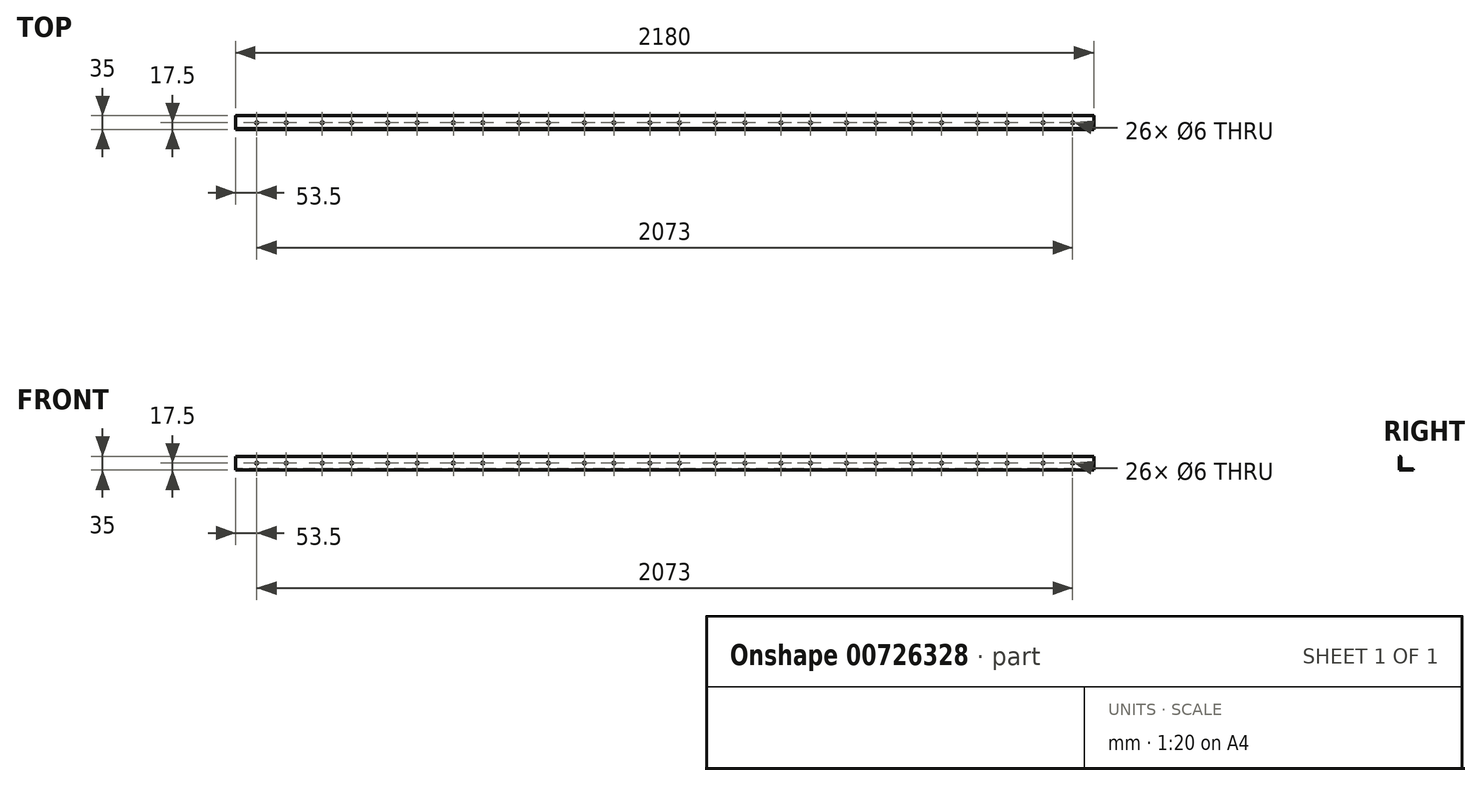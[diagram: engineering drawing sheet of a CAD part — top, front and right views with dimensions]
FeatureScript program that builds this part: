
annotation { "Feature Type Name" : "Feature", "Feature Type Description" : "" }
export const myFeature = defineFeature(function(context is Context, id is Id, definition is map)
    precondition{}
    {
        {
            var Q0;
            Q0=qCreatedBy(makeId("Right.planeOp"),FACE);
            var sketch = newSketch(context, id + "F0", { "sketchPlane" : qUnion([Q0])});
            skLineSegment(sketch, "E0", {"start": v(0, 0) * mm, "end": v(35, 0) * mm});
            skLineSegment(sketch, "E1", {"start": v(35, 0) * mm, "end": v(35, 1) * mm});
            skLineSegment(sketch, "E2", {"start": v(33, 3) * mm, "end": v(6.5, 3) * mm});
            skLineSegment(sketch, "E3", {"start": v(3, 6.5) * mm, "end": v(3, 33) * mm});
            skLineSegment(sketch, "E4", {"start": v(1, 35) * mm, "end": v(0, 35) * mm});
            skLineSegment(sketch, "E5", {"start": v(0, 35) * mm, "end": v(0, 0) * mm});
            skPoint(sketch, "E6.visualSharp", {"position": v(3, 3) * mm});
            skArc(sketch, "E6.filletArc", {"start": v(3, 6.5) * mm, "mid": v(4.03, 4.03) * mm, "end": v(6.5, 3) * mm});
            skPoint(sketch, "E7.visualSharp", {"position": v(35, 3) * mm});
            skArc(sketch, "E7.filletArc", {"start": v(35, 1) * mm, "mid": v(34.41, 2.41) * mm, "end": v(33, 3) * mm});
            skPoint(sketch, "E8.visualSharp", {"position": v(3, 35) * mm});
            skArc(sketch, "E8.filletArc", {"start": v(3, 33) * mm, "mid": v(2.41, 34.41) * mm, "end": v(1, 35) * mm});
            skSolve(sketch);
        }
        {
            var Q0;
            Q0=makeQuery(id+"F0.imprint","IMPRINT",FACE,{"disambiguationData":[TD([[makeQuery(id+"F0.imprint","IMPRINT",EDGE,{"derivedFrom":sQuery(id+"F0.wireOp",EDGE,"E0")}),1.0]])]});
            extrude(context, id + "F1", {"entities" : qUnion([Q0]), "depth" : 1090 * mm, "offsetDistance" : 25 * mm, "hasSecondDirection" : true, "secondDirectionOppositeDirection" : true, "secondDirectionDepth" : 1090 * mm});
        }
        {
            var Q0;
            Q0=makeQuery(id+"F1.opExtrude","SWEPT_FACE",FACE,{"disambiguationData":[OSD([sQuery(id+"F0.wireOp",EDGE,"E5")])]});
            var sketch = newSketch(context, id + "F2", { "sketchPlane" : qUnion([Q0])});
            skCircle(sketch, "E9", {"center": v(-1036.5, 17.5) * mm, "radius": 3 * mm});
            skPoint(sketch, "E9.centerSnap0", {"position": v(-1090, 17.5) * mm});
            skCircle(sketch, "E10", {"center": v(-961.5, 17.5) * mm, "radius": 3 * mm});
            skLineSegment(sketch, "E11", {"start": v(-1090, 17.5) * mm, "end": v(1106.3, 17.5) * mm, "construction": true});
            skLineSegment(sketch, "E12", {"start": v(-1074, 24.24) * mm, "end": v(-1074, 8.1) * mm, "construction": true});
            skLineSegment(sketch, "E13", {"start": v(-999, 40.12) * mm, "end": v(-999, -7.77) * mm, "construction": true});
            skLineSegment(sketch, "E14", {"start": v(-924, 26.27) * mm, "end": v(-924, 4.37) * mm});
            skLineSegment(sketch, "E15", {"start": v(-907.5, 23.5) * mm, "end": v(-907.5, 9.52) * mm});
            skCircle(sketch, "E16.1.0.0", {"center": v(-870, 17.5) * mm, "radius": 3 * mm});
            skCircle(sketch, "E16.1.0.1", {"center": v(-795, 17.5) * mm, "radius": 3 * mm});
            skCircle(sketch, "E16.2.0.0", {"center": v(-703.5, 17.5) * mm, "radius": 3 * mm});
            skCircle(sketch, "E16.2.0.1", {"center": v(-628.5, 17.5) * mm, "radius": 3 * mm});
            skCircle(sketch, "E16.3.0.0", {"center": v(-537, 17.5) * mm, "radius": 3 * mm});
            skCircle(sketch, "E16.3.0.1", {"center": v(-462, 17.5) * mm, "radius": 3 * mm});
            skCircle(sketch, "E16.4.0.0", {"center": v(-370.5, 17.5) * mm, "radius": 3 * mm});
            skCircle(sketch, "E16.4.0.1", {"center": v(-295.5, 17.5) * mm, "radius": 3 * mm});
            skCircle(sketch, "E16.5.0.0", {"center": v(-204, 17.5) * mm, "radius": 3 * mm});
            skCircle(sketch, "E16.5.0.1", {"center": v(-129, 17.5) * mm, "radius": 3 * mm});
            skCircle(sketch, "E16.6.0.0", {"center": v(-37.5, 17.5) * mm, "radius": 3 * mm});
            skCircle(sketch, "E16.6.0.1", {"center": v(37.5, 17.5) * mm, "radius": 3 * mm});
            skCircle(sketch, "E16.7.0.0", {"center": v(129, 17.5) * mm, "radius": 3 * mm});
            skCircle(sketch, "E16.7.0.1", {"center": v(204, 17.5) * mm, "radius": 3 * mm});
            skCircle(sketch, "E16.8.0.0", {"center": v(295.5, 17.5) * mm, "radius": 3 * mm});
            skCircle(sketch, "E16.8.0.1", {"center": v(370.5, 17.5) * mm, "radius": 3 * mm});
            skCircle(sketch, "E16.9.0.0", {"center": v(462, 17.5) * mm, "radius": 3 * mm});
            skCircle(sketch, "E16.9.0.1", {"center": v(537, 17.5) * mm, "radius": 3 * mm});
            skCircle(sketch, "E16.10.0.0", {"center": v(628.5, 17.5) * mm, "radius": 3 * mm});
            skCircle(sketch, "E16.10.0.1", {"center": v(703.5, 17.5) * mm, "radius": 3 * mm});
            skCircle(sketch, "E16.11.0.0", {"center": v(795, 17.5) * mm, "radius": 3 * mm});
            skCircle(sketch, "E16.11.0.1", {"center": v(870, 17.5) * mm, "radius": 3 * mm});
            skCircle(sketch, "E16.12.0.0", {"center": v(961.5, 17.5) * mm, "radius": 3 * mm});
            skCircle(sketch, "E16.12.0.1", {"center": v(1036.5, 17.5) * mm, "radius": 3 * mm});
            skCircle(sketch, "E16.13.0.0", {"center": v(1128, 17.5) * mm, "radius": 3 * mm});
            skCircle(sketch, "E16.13.0.1", {"center": v(1203, 17.5) * mm, "radius": 3 * mm});
            skCircle(sketch, "E16.14.0.0", {"center": v(1294.5, 17.5) * mm, "radius": 3 * mm});
            skCircle(sketch, "E16.14.0.1", {"center": v(1369.5, 17.5) * mm, "radius": 3 * mm});
            skCircle(sketch, "E16.15.0.0", {"center": v(1461, 17.5) * mm, "radius": 3 * mm});
            skCircle(sketch, "E16.15.0.1", {"center": v(1536, 17.5) * mm, "radius": 3 * mm});
            skCircle(sketch, "E16.16.0.0", {"center": v(1627.5, 17.5) * mm, "radius": 3 * mm});
            skCircle(sketch, "E16.16.0.1", {"center": v(1702.5, 17.5) * mm, "radius": 3 * mm});
            skCircle(sketch, "E16.17.0.0", {"center": v(1794, 17.5) * mm, "radius": 3 * mm});
            skCircle(sketch, "E16.17.0.1", {"center": v(1869, 17.5) * mm, "radius": 3 * mm});
            skCircle(sketch, "E16.18.0.0", {"center": v(1960.5, 17.5) * mm, "radius": 3 * mm});
            skCircle(sketch, "E16.18.0.1", {"center": v(2035.5, 17.5) * mm, "radius": 3 * mm});
            skCircle(sketch, "E16.19.0.0", {"center": v(2127, 17.5) * mm, "radius": 3 * mm});
            skCircle(sketch, "E16.19.0.1", {"center": v(2202, 17.5) * mm, "radius": 3 * mm});
            skLineSegment(sketch, "E16.direction1", {"start": v(-1036.5, 17.5) * mm, "end": v(-870, 17.5) * mm, "construction": true});
            skSolve(sketch);
        }
        {
            var Q0;
            Q0=makeQuery(id+"F2.imprint","IMPRINT",FACE,{"disambiguationData":[TD([[makeQuery(id+"F2.imprint","IMPRINT",EDGE,{"derivedFrom":sQuery(id+"F2.wireOp",EDGE,"E16.13.0.0")}),1.0]])]});
            var Q1;
            Q1=makeQuery(id+"F2.imprint","IMPRINT",FACE,{"disambiguationData":[TD([[makeQuery(id+"F2.imprint","IMPRINT",EDGE,{"derivedFrom":sQuery(id+"F2.wireOp",EDGE,"E16.13.0.1")}),1.0]])]});
            var Q2;
            Q2=makeQuery(id+"F2.imprint","IMPRINT",FACE,{"disambiguationData":[TD([[makeQuery(id+"F2.imprint","IMPRINT",EDGE,{"derivedFrom":sQuery(id+"F2.wireOp",EDGE,"E16.14.0.0")}),1.0]])]});
            var Q3;
            Q3=makeQuery(id+"F2.imprint","IMPRINT",FACE,{"disambiguationData":[TD([[makeQuery(id+"F2.imprint","IMPRINT",EDGE,{"derivedFrom":sQuery(id+"F2.wireOp",EDGE,"E16.14.0.1")}),1.0]])]});
            var Q4;
            Q4=makeQuery(id+"F2.imprint","IMPRINT",FACE,{"disambiguationData":[TD([[makeQuery(id+"F2.imprint","IMPRINT",EDGE,{"derivedFrom":sQuery(id+"F2.wireOp",EDGE,"E16.15.0.0")}),1.0]])]});
            var Q5;
            Q5=makeQuery(id+"F2.imprint","IMPRINT",FACE,{"disambiguationData":[TD([[makeQuery(id+"F2.imprint","IMPRINT",EDGE,{"derivedFrom":sQuery(id+"F2.wireOp",EDGE,"E16.15.0.1")}),1.0]])]});
            var Q6;
            Q6=makeQuery(id+"F2.imprint","IMPRINT",FACE,{"disambiguationData":[TD([[makeQuery(id+"F2.imprint","IMPRINT",EDGE,{"derivedFrom":sQuery(id+"F2.wireOp",EDGE,"E16.16.0.0")}),1.0]])]});
            var Q7;
            Q7=makeQuery(id+"F2.imprint","IMPRINT",FACE,{"disambiguationData":[TD([[makeQuery(id+"F2.imprint","IMPRINT",EDGE,{"derivedFrom":sQuery(id+"F2.wireOp",EDGE,"E16.16.0.1")}),1.0]])]});
            var Q8;
            Q8=makeQuery(id+"F2.imprint","IMPRINT",FACE,{"disambiguationData":[TD([[makeQuery(id+"F2.imprint","IMPRINT",EDGE,{"derivedFrom":sQuery(id+"F2.wireOp",EDGE,"E16.17.0.0")}),1.0]])]});
            var Q9;
            Q9=makeQuery(id+"F2.imprint","IMPRINT",FACE,{"disambiguationData":[TD([[makeQuery(id+"F2.imprint","IMPRINT",EDGE,{"derivedFrom":sQuery(id+"F2.wireOp",EDGE,"E16.17.0.1")}),1.0]])]});
            var Q10;
            Q10=makeQuery(id+"F2.imprint","IMPRINT",FACE,{"disambiguationData":[TD([[makeQuery(id+"F2.imprint","IMPRINT",EDGE,{"derivedFrom":sQuery(id+"F2.wireOp",EDGE,"E16.18.0.0")}),1.0]])]});
            var Q11;
            Q11=makeQuery(id+"F2.imprint","IMPRINT",FACE,{"disambiguationData":[TD([[makeQuery(id+"F2.imprint","IMPRINT",EDGE,{"derivedFrom":sQuery(id+"F2.wireOp",EDGE,"E16.18.0.1")}),1.0]])]});
            var Q12;
            Q12=makeQuery(id+"F2.imprint","IMPRINT",FACE,{"disambiguationData":[TD([[makeQuery(id+"F2.imprint","IMPRINT",EDGE,{"derivedFrom":sQuery(id+"F2.wireOp",EDGE,"E16.19.0.0")}),1.0]])]});
            var Q13;
            Q13=makeQuery(id+"F2.imprint","IMPRINT",FACE,{"disambiguationData":[TD([[makeQuery(id+"F2.imprint","IMPRINT",EDGE,{"derivedFrom":sQuery(id+"F2.wireOp",EDGE,"E16.19.0.1")}),1.0]])]});
            var Q14;
            Q14=makeQuery(id+"F2.imprint","IMPRINT",FACE,{"disambiguationData":[TD([[makeQuery(id+"F2.imprint","IMPRINT",EDGE,{"derivedFrom":sQuery(id+"F2.wireOp",EDGE,"E10")}),1.0]])]});
            var Q15;
            Q15=makeQuery(id+"F2.imprint","IMPRINT",FACE,{"disambiguationData":[TD([[makeQuery(id+"F2.imprint","IMPRINT",EDGE,{"derivedFrom":sQuery(id+"F2.wireOp",EDGE,"E16.1.0.0")}),1.0]])]});
            var Q16;
            Q16=makeQuery(id+"F2.imprint","IMPRINT",FACE,{"disambiguationData":[TD([[makeQuery(id+"F2.imprint","IMPRINT",EDGE,{"derivedFrom":sQuery(id+"F2.wireOp",EDGE,"E16.1.0.1")}),1.0]])]});
            var Q17;
            Q17=makeQuery(id+"F2.imprint","IMPRINT",FACE,{"disambiguationData":[TD([[makeQuery(id+"F2.imprint","IMPRINT",EDGE,{"derivedFrom":sQuery(id+"F2.wireOp",EDGE,"E16.2.0.0")}),1.0]])]});
            var Q18;
            Q18=makeQuery(id+"F2.imprint","IMPRINT",FACE,{"disambiguationData":[TD([[makeQuery(id+"F2.imprint","IMPRINT",EDGE,{"derivedFrom":sQuery(id+"F2.wireOp",EDGE,"E16.2.0.1")}),1.0]])]});
            var Q19;
            Q19=makeQuery(id+"F2.imprint","IMPRINT",FACE,{"disambiguationData":[TD([[makeQuery(id+"F2.imprint","IMPRINT",EDGE,{"derivedFrom":sQuery(id+"F2.wireOp",EDGE,"E16.3.0.0")}),1.0]])]});
            var Q20;
            Q20=makeQuery(id+"F2.imprint","IMPRINT",FACE,{"disambiguationData":[TD([[makeQuery(id+"F2.imprint","IMPRINT",EDGE,{"derivedFrom":sQuery(id+"F2.wireOp",EDGE,"E16.3.0.1")}),1.0]])]});
            var Q21;
            Q21=makeQuery(id+"F2.imprint","IMPRINT",FACE,{"disambiguationData":[TD([[makeQuery(id+"F2.imprint","IMPRINT",EDGE,{"derivedFrom":sQuery(id+"F2.wireOp",EDGE,"E16.4.0.0")}),1.0]])]});
            var Q22;
            Q22=makeQuery(id+"F2.imprint","IMPRINT",FACE,{"disambiguationData":[TD([[makeQuery(id+"F2.imprint","IMPRINT",EDGE,{"derivedFrom":sQuery(id+"F2.wireOp",EDGE,"E16.4.0.1")}),1.0]])]});
            var Q23;
            Q23=makeQuery(id+"F2.imprint","IMPRINT",FACE,{"disambiguationData":[TD([[makeQuery(id+"F2.imprint","IMPRINT",EDGE,{"derivedFrom":sQuery(id+"F2.wireOp",EDGE,"E16.5.0.0")}),1.0]])]});
            var Q24;
            Q24=makeQuery(id+"F2.imprint","IMPRINT",FACE,{"disambiguationData":[TD([[makeQuery(id+"F2.imprint","IMPRINT",EDGE,{"derivedFrom":sQuery(id+"F2.wireOp",EDGE,"E16.5.0.1")}),1.0]])]});
            var Q25;
            Q25=makeQuery(id+"F2.imprint","IMPRINT",FACE,{"disambiguationData":[TD([[makeQuery(id+"F2.imprint","IMPRINT",EDGE,{"derivedFrom":sQuery(id+"F2.wireOp",EDGE,"E16.6.0.0")}),1.0]])]});
            var Q26;
            Q26=makeQuery(id+"F2.imprint","IMPRINT",FACE,{"disambiguationData":[TD([[makeQuery(id+"F2.imprint","IMPRINT",EDGE,{"derivedFrom":sQuery(id+"F2.wireOp",EDGE,"E16.6.0.1")}),1.0]])]});
            var Q27;
            Q27=makeQuery(id+"F2.imprint","IMPRINT",FACE,{"disambiguationData":[TD([[makeQuery(id+"F2.imprint","IMPRINT",EDGE,{"derivedFrom":sQuery(id+"F2.wireOp",EDGE,"E16.7.0.0")}),1.0]])]});
            var Q28;
            Q28=makeQuery(id+"F2.imprint","IMPRINT",FACE,{"disambiguationData":[TD([[makeQuery(id+"F2.imprint","IMPRINT",EDGE,{"derivedFrom":sQuery(id+"F2.wireOp",EDGE,"E16.7.0.1")}),1.0]])]});
            var Q29;
            Q29=makeQuery(id+"F2.imprint","IMPRINT",FACE,{"disambiguationData":[TD([[makeQuery(id+"F2.imprint","IMPRINT",EDGE,{"derivedFrom":sQuery(id+"F2.wireOp",EDGE,"E16.8.0.0")}),1.0]])]});
            var Q30;
            Q30=makeQuery(id+"F2.imprint","IMPRINT",FACE,{"disambiguationData":[TD([[makeQuery(id+"F2.imprint","IMPRINT",EDGE,{"derivedFrom":sQuery(id+"F2.wireOp",EDGE,"E16.8.0.1")}),1.0]])]});
            var Q31;
            Q31=makeQuery(id+"F2.imprint","IMPRINT",FACE,{"disambiguationData":[TD([[makeQuery(id+"F2.imprint","IMPRINT",EDGE,{"derivedFrom":sQuery(id+"F2.wireOp",EDGE,"E16.9.0.0")}),1.0]])]});
            var Q32;
            Q32=makeQuery(id+"F2.imprint","IMPRINT",FACE,{"disambiguationData":[TD([[makeQuery(id+"F2.imprint","IMPRINT",EDGE,{"derivedFrom":sQuery(id+"F2.wireOp",EDGE,"E16.9.0.1")}),1.0]])]});
            var Q33;
            Q33=makeQuery(id+"F2.imprint","IMPRINT",FACE,{"disambiguationData":[TD([[makeQuery(id+"F2.imprint","IMPRINT",EDGE,{"derivedFrom":sQuery(id+"F2.wireOp",EDGE,"E16.10.0.0")}),1.0]])]});
            var Q34;
            Q34=makeQuery(id+"F2.imprint","IMPRINT",FACE,{"disambiguationData":[TD([[makeQuery(id+"F2.imprint","IMPRINT",EDGE,{"derivedFrom":sQuery(id+"F2.wireOp",EDGE,"E16.10.0.1")}),1.0]])]});
            var Q35;
            Q35=makeQuery(id+"F2.imprint","IMPRINT",FACE,{"disambiguationData":[TD([[makeQuery(id+"F2.imprint","IMPRINT",EDGE,{"derivedFrom":sQuery(id+"F2.wireOp",EDGE,"E16.11.0.0")}),1.0]])]});
            var Q36;
            Q36=makeQuery(id+"F2.imprint","IMPRINT",FACE,{"disambiguationData":[TD([[makeQuery(id+"F2.imprint","IMPRINT",EDGE,{"derivedFrom":sQuery(id+"F2.wireOp",EDGE,"E16.11.0.1")}),1.0]])]});
            var Q37;
            Q37=makeQuery(id+"F2.imprint","IMPRINT",FACE,{"disambiguationData":[TD([[makeQuery(id+"F2.imprint","IMPRINT",EDGE,{"derivedFrom":sQuery(id+"F2.wireOp",EDGE,"E16.12.0.0")}),1.0]])]});
            var Q38;
            Q38=makeQuery(id+"F2.imprint","IMPRINT",FACE,{"disambiguationData":[TD([[makeQuery(id+"F2.imprint","IMPRINT",EDGE,{"derivedFrom":sQuery(id+"F2.wireOp",EDGE,"E16.12.0.1")}),1.0]])]});
            var Q39;
            Q39=makeQuery(id+"F2.imprint","IMPRINT",FACE,{"disambiguationData":[TD([[makeQuery(id+"F2.imprint","IMPRINT",EDGE,{"derivedFrom":sQuery(id+"F2.wireOp",EDGE,"E9")}),1.0]])]});
            extrude(context, id + "F3", {"entities" : qUnion([Q0, Q1, Q2, Q3, Q4, Q5, Q6, Q7, Q8, Q9, Q10, Q11, Q12, Q13, Q14, Q15, Q16, Q17, Q18, Q19, Q20, Q21, Q22, Q23, Q24, Q25, Q26, Q27, Q28, Q29, Q30, Q31, Q32, Q33, Q34, Q35, Q36, Q37, Q38, Q39]), "operationType" : NewBodyOperationType.REMOVE, "oppositeDirection" : true, "depth" : 25 * mm, "offsetDistance" : 25 * mm});
        }
        {
            var Q0;
            Q0=makeQuery(id+"F1.opExtrude","SWEPT_FACE",FACE,{"disambiguationData":[OSD([sQuery(id+"F0.wireOp",EDGE,"E0")])]});
            var sketch = newSketch(context, id + "F4", { "sketchPlane" : qUnion([Q0])});
            skCircle(sketch, "E17", {"center": v(-1036.5, -17.5) * mm, "radius": 3 * mm});
            skPoint(sketch, "E17.centerSnap0", {"position": v(-1090, -17.5) * mm});
            skCircle(sketch, "E18", {"center": v(-961.5, -17.5) * mm, "radius": 3 * mm});
            skCircle(sketch, "E19.1.0.0", {"center": v(-870, -17.5) * mm, "radius": 3 * mm});
            skCircle(sketch, "E19.1.0.1", {"center": v(-795, -17.5) * mm, "radius": 3 * mm});
            skCircle(sketch, "E19.2.0.0", {"center": v(-703.5, -17.5) * mm, "radius": 3 * mm});
            skCircle(sketch, "E19.2.0.1", {"center": v(-628.5, -17.5) * mm, "radius": 3 * mm});
            skCircle(sketch, "E19.3.0.0", {"center": v(-537, -17.5) * mm, "radius": 3 * mm});
            skCircle(sketch, "E19.3.0.1", {"center": v(-462, -17.5) * mm, "radius": 3 * mm});
            skCircle(sketch, "E19.4.0.0", {"center": v(-370.5, -17.5) * mm, "radius": 3 * mm});
            skCircle(sketch, "E19.4.0.1", {"center": v(-295.5, -17.5) * mm, "radius": 3 * mm});
            skCircle(sketch, "E19.5.0.0", {"center": v(-204, -17.5) * mm, "radius": 3 * mm});
            skCircle(sketch, "E19.5.0.1", {"center": v(-129, -17.5) * mm, "radius": 3 * mm});
            skCircle(sketch, "E19.6.0.0", {"center": v(-37.5, -17.5) * mm, "radius": 3 * mm});
            skCircle(sketch, "E19.6.0.1", {"center": v(37.5, -17.5) * mm, "radius": 3 * mm});
            skCircle(sketch, "E19.7.0.0", {"center": v(129, -17.5) * mm, "radius": 3 * mm});
            skCircle(sketch, "E19.7.0.1", {"center": v(204, -17.5) * mm, "radius": 3 * mm});
            skCircle(sketch, "E19.8.0.0", {"center": v(295.5, -17.5) * mm, "radius": 3 * mm});
            skCircle(sketch, "E19.8.0.1", {"center": v(370.5, -17.5) * mm, "radius": 3 * mm});
            skCircle(sketch, "E19.9.0.0", {"center": v(462, -17.5) * mm, "radius": 3 * mm});
            skCircle(sketch, "E19.9.0.1", {"center": v(537, -17.5) * mm, "radius": 3 * mm});
            skCircle(sketch, "E19.10.0.0", {"center": v(628.5, -17.5) * mm, "radius": 3 * mm});
            skCircle(sketch, "E19.10.0.1", {"center": v(703.5, -17.5) * mm, "radius": 3 * mm});
            skCircle(sketch, "E19.11.0.0", {"center": v(795, -17.5) * mm, "radius": 3 * mm});
            skCircle(sketch, "E19.11.0.1", {"center": v(870, -17.5) * mm, "radius": 3 * mm});
            skCircle(sketch, "E19.12.0.0", {"center": v(961.5, -17.5) * mm, "radius": 3 * mm});
            skCircle(sketch, "E19.12.0.1", {"center": v(1036.5, -17.5) * mm, "radius": 3 * mm});
            skCircle(sketch, "E19.13.0.0", {"center": v(1128, -17.5) * mm, "radius": 3 * mm});
            skCircle(sketch, "E19.13.0.1", {"center": v(1203, -17.5) * mm, "radius": 3 * mm});
            skCircle(sketch, "E19.14.0.0", {"center": v(1294.5, -17.5) * mm, "radius": 3 * mm});
            skCircle(sketch, "E19.14.0.1", {"center": v(1369.5, -17.5) * mm, "radius": 3 * mm});
            skCircle(sketch, "E19.15.0.0", {"center": v(1461, -17.5) * mm, "radius": 3 * mm});
            skCircle(sketch, "E19.15.0.1", {"center": v(1536, -17.5) * mm, "radius": 3 * mm});
            skCircle(sketch, "E19.16.0.0", {"center": v(1627.5, -17.5) * mm, "radius": 3 * mm});
            skCircle(sketch, "E19.16.0.1", {"center": v(1702.5, -17.5) * mm, "radius": 3 * mm});
            skCircle(sketch, "E19.17.0.0", {"center": v(1794, -17.5) * mm, "radius": 3 * mm});
            skCircle(sketch, "E19.17.0.1", {"center": v(1869, -17.5) * mm, "radius": 3 * mm});
            skCircle(sketch, "E19.18.0.0", {"center": v(1960.5, -17.5) * mm, "radius": 3 * mm});
            skCircle(sketch, "E19.18.0.1", {"center": v(2035.5, -17.5) * mm, "radius": 3 * mm});
            skCircle(sketch, "E19.19.0.0", {"center": v(2127, -17.5) * mm, "radius": 3 * mm});
            skCircle(sketch, "E19.19.0.1", {"center": v(2202, -17.5) * mm, "radius": 3 * mm});
            skLineSegment(sketch, "E19.direction1", {"start": v(-1036.5, -17.5) * mm, "end": v(-870, -17.5) * mm, "construction": true});
            skSolve(sketch);
        }
        {
            var Q0;
            Q0 = qSketchRegion(id + "F4", true);
            extrude(context, id + "F5", {"entities" : qUnion([Q0]), "operationType" : NewBodyOperationType.REMOVE, "oppositeDirection" : true, "depth" : 25 * mm, "offsetDistance" : 25 * mm});
        }
    });
